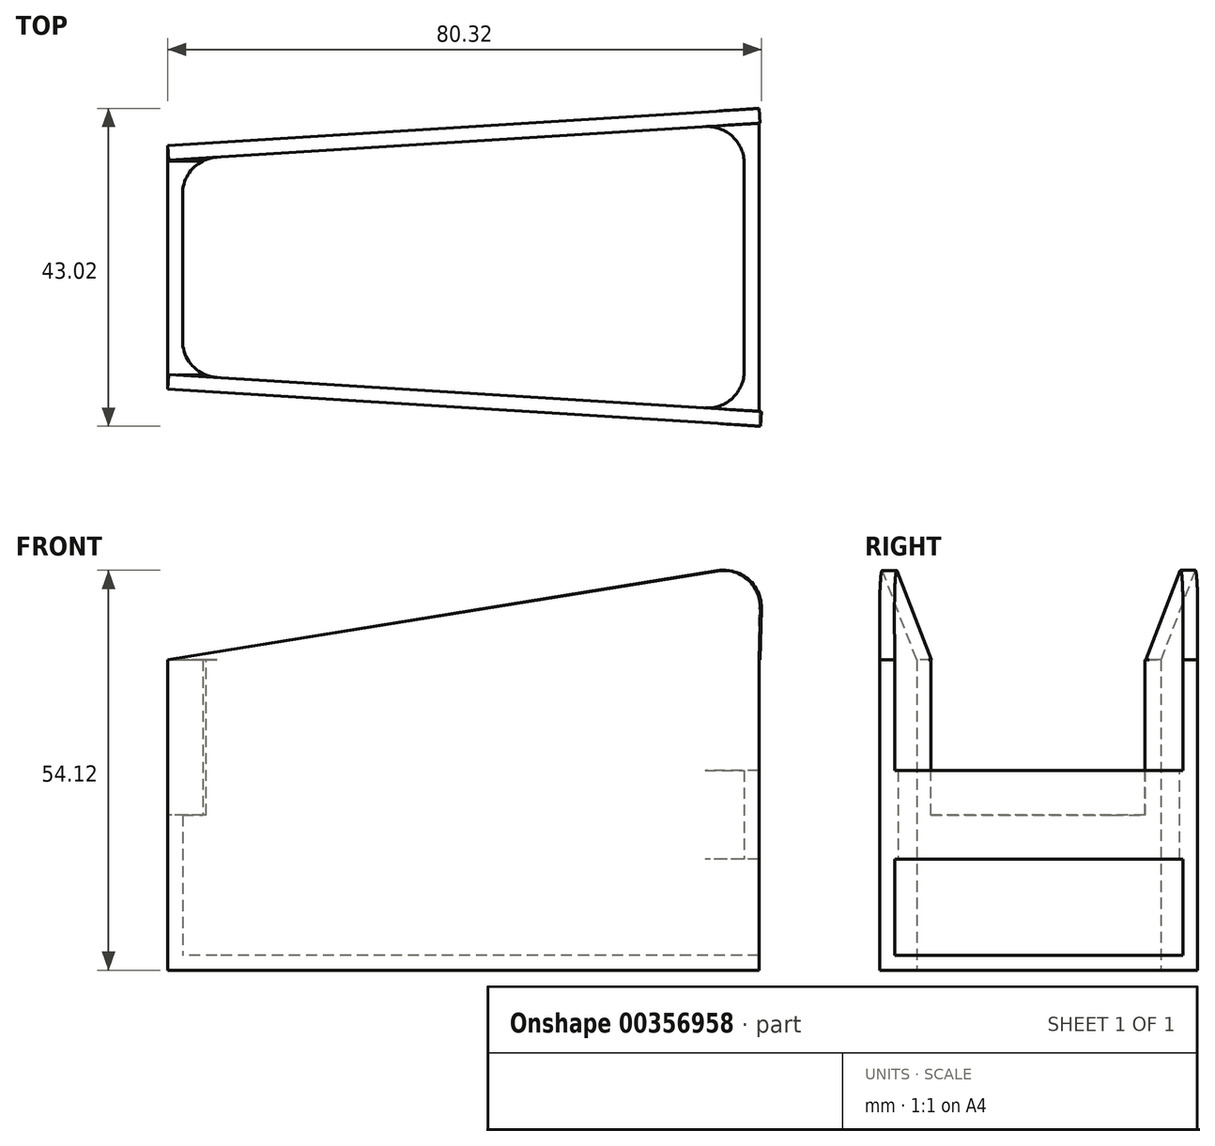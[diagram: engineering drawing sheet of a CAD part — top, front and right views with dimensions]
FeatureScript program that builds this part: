
annotation { "Feature Type Name" : "Feature", "Feature Type Description" : "" }
export const myFeature = defineFeature(function(context is Context, id is Id, definition is map)
    precondition{}
    {
        {
            var Q0;
            Q0=qCreatedBy(makeId("Top.planeOp"),FACE);
            var sketch = newSketch(context, id + "F0", { "sketchPlane" : qUnion([Q0])});
            skLineSegment(sketch, "E0", {"start": v(-65.37, 35.18) * mm, "end": v(-2.44, 35.18) * mm, "construction": true});
            skLineSegment(sketch, "E1", {"start": v(18.9, 56.68) * mm, "end": v(18.9, 13.68) * mm, "construction": true});
            skLineSegment(sketch, "E2", {"start": v(-61.1, 51.68) * mm, "end": v(-61.1, 18.68) * mm, "construction": true});
            skLineSegment(sketch, "E3", {"start": v(-2.44, 35.18) * mm, "end": v(28.85, 35.18) * mm, "construction": true});
            skLineSegment(sketch, "E4", {"start": v(-61.1, 51.68) * mm, "end": v(18.9, 56.68) * mm});
            skLineSegment(sketch, "E5", {"start": v(18.9, 56.68) * mm, "end": v(18.9, 13.68) * mm});
            skLineSegment(sketch, "E6", {"start": v(-61.1, 18.68) * mm, "end": v(18.9, 13.68) * mm});
            skLineSegment(sketch, "E7", {"start": v(-61.1, 51.68) * mm, "end": v(-61.1, 18.68) * mm});
            skLineSegment(sketch, "E8.0", {"start": v(-60.97, 49.68) * mm, "end": v(19.03, 54.68) * mm, "construction": true});
            skLineSegment(sketch, "E9.0", {"start": v(-60.97, 20.67) * mm, "end": v(19.03, 15.67) * mm});
            skLineSegment(sketch, "E10.0", {"start": v(16.9, 56.68) * mm, "end": v(16.9, 56.55) * mm});
            skLineSegment(sketch, "E11.0", {"start": v(-59.1, 49.8) * mm, "end": v(-59.1, 20.56) * mm});
            skLineSegment(sketch, "E12", {"start": v(-59.1, 49.8) * mm, "end": v(16.9, 54.55) * mm});
            skLineSegment(sketch, "E13.trimOffspring", {"start": v(16.9, 54.55) * mm, "end": v(16.9, 15.8) * mm});
            skLineSegment(sketch, "E14.trimOffspring", {"start": v(16.9, 13.8) * mm, "end": v(16.9, 13.68) * mm});
            skLineSegment(sketch, "E15", {"start": v(16.9, 54.55) * mm, "end": v(19.03, 54.68) * mm});
            skLineSegment(sketch, "E16", {"start": v(-59.1, 49.8) * mm, "end": v(-60.97, 49.68) * mm});
            skSolve(sketch);
        }
        {
            var Q0;
            {var subQ6=sQuery(id+"F0.wireOp",EDGE,"E7");Q0=makeQuery(id+"F0.imprint","IMPRINT",FACE,{"disambiguationData":[TD([[makeQuery(id+"F0.imprint","IMPRINT",EDGE,{"derivedFrom":subQ6}),1.0]])]});}
            var Q1;
            {var subQ5=sQuery(id+"F0.wireOp",EDGE,"E13.trimOffspring");Q1=makeQuery(id+"F0.imprint","IMPRINT",FACE,{"disambiguationData":[TD([[makeQuery(id+"F0.imprint","IMPRINT",EDGE,{"derivedFrom":subQ5}),1.0]])]});}
            var Q2;
            {var subQ0=sQuery(id+"F0.wireOp",EDGE,"E11.0");Q2=makeQuery(id+"F0.imprint","IMPRINT",FACE,{"disambiguationData":[TD([[makeQuery(id+"F0.imprint","IMPRINT",EDGE,{"derivedFrom":subQ0}),1.0]])]});}
            extrude(context, id + "F1", {"entities" : qUnion([Q0, Q1, Q2]), "depth" : 2 * mm, "offsetDistance" : 25 * mm});
        }
        {
            var Q0;
            {var subQ6=sQuery(id+"F0.wireOp",EDGE,"E7");Q0=makeQuery(id+"F0.imprint","IMPRINT",FACE,{"disambiguationData":[TD([[makeQuery(id+"F0.imprint","IMPRINT",EDGE,{"derivedFrom":subQ6}),1.0]])]});}
            extrude(context, id + "F2", {"entities" : qUnion([Q0]), "operationType" : NewBodyOperationType.ADD, "depth" : 42 * mm, "offsetDistance" : 25 * mm});
        }
        {
            var Q0;
            {var subQ0=sQuery(id+"F0.wireOp",EDGE,"E6");Q0=makeQuery(id+"F2.boolean.opBoolean","MERGE",FACE,{"derivedFrom":[makeQuery(id+"F1.opExtrude","SWEPT_FACE",FACE,{"disambiguationData":[OSD([subQ0])]}),makeQuery(id+"F2.opExtrude","SWEPT_FACE",FACE,{"disambiguationData":[OSD([subQ0])]})]});}
            var sketch = newSketch(context, id + "F3", { "sketchPlane" : qUnion([Q0])});
            skLineSegment(sketch, "E17", {"start": v(-62.15, 42) * mm, "end": v(18.37, 55) * mm});
            skLineSegment(sketch, "E18", {"start": v(18.01, 42) * mm, "end": v(18.37, 55) * mm});
            skLineSegment(sketch, "E19", {"start": v(18.37, 55) * mm, "end": v(18.01, 0) * mm, "construction": true});
            skSolve(sketch);
        }
        {
            var Q0;
            {var subQ0=sQuery(id+"F0.wireOp",EDGE,"E5");Q0=makeQuery(id+"F2.boolean.opBoolean","MERGE",FACE,{"derivedFrom":[makeQuery(id+"F1.opExtrude","SWEPT_FACE",FACE,{"disambiguationData":[OSD([subQ0])]}),makeQuery(id+"F2.opExtrude","SWEPT_FACE",FACE,{"disambiguationData":[OSD([subQ0]),TDD([makeQuery(id+"F0.imprint","IMPRINT",EDGE,{"disambiguationData":[TD([[makeQuery(id+"F0.imprint","INTERSECT",VERTEX,{"derivedFrom":[sQuery(id+"F0.wireOp",EDGE,"E4"),subQ0]}),-1.0]])],"derivedFrom":subQ0})])]}),makeQuery(id+"F2.opExtrude","SWEPT_FACE",FACE,{"disambiguationData":[OSD([subQ0]),TDD([makeQuery(id+"F0.imprint","IMPRINT",EDGE,{"disambiguationData":[TD([[makeQuery(id+"F0.imprint","INTERSECT",VERTEX,{"derivedFrom":[subQ0,sQuery(id+"F0.wireOp",EDGE,"E6")]}),1.0]])],"derivedFrom":subQ0})])]})]});}
            var sketch = newSketch(context, id + "F4", { "sketchPlane" : qUnion([Q0])});
            skLineSegment(sketch, "E20", {"start": v(13.68, 42) * mm, "end": v(15.68, 42) * mm});
            skLineSegment(sketch, "E21", {"start": v(13.68, 62.32) * mm, "end": v(13.68, 42) * mm});
            skSolve(sketch);
        }
        {
            var Q0;
            Q0=makeQuery(id+"F3.imprint","IMPRINT",FACE,{"disambiguationData":[TD([[makeQuery(id+"F3.imprint","IMPRINT",EDGE,{"derivedFrom":sQuery(id+"F3.wireOp",EDGE,"E17")}),-1.0]])]});
            extrude(context, id + "F5", {"entities" : qUnion([Q0]), "operationType" : NewBodyOperationType.ADD, "oppositeDirection" : true, "depth" : 2 * mm, "offsetDistance" : 25 * mm});
        }
        {
            var Q0;
            {var subQ0=sQuery(id+"F0.wireOp",EDGE,"E4");Q0=makeQuery(id+"F2.boolean.opBoolean","MERGE",FACE,{"derivedFrom":[makeQuery(id+"F1.opExtrude","SWEPT_FACE",FACE,{"disambiguationData":[OSD([subQ0])]}),makeQuery(id+"F2.opExtrude","SWEPT_FACE",FACE,{"disambiguationData":[OSD([subQ0])]})]});}
            var sketch = newSketch(context, id + "F6", { "sketchPlane" : qUnion([Q0])});
            skLineSegment(sketch, "E22", {"start": v(-22.4, 42) * mm, "end": v(-22.4, 55) * mm});
            skLineSegment(sketch, "E23", {"start": v(-22.4, 55) * mm, "end": v(57.76, 42) * mm});
            skSolve(sketch);
        }
        {
            var Q0;
            Q0=makeQuery(id+"F6.imprint","IMPRINT",FACE,{"disambiguationData":[TD([[makeQuery(id+"F6.imprint","IMPRINT",EDGE,{"derivedFrom":sQuery(id+"F6.wireOp",EDGE,"E22")}),-1.0]])]});
            extrude(context, id + "F7", {"entities" : qUnion([Q0]), "operationType" : NewBodyOperationType.ADD, "oppositeDirection" : true, "depth" : 2 * mm, "offsetDistance" : 25 * mm});
        }
        {
            var Q0;
            {var subQ0=sQuery(id+"F0.wireOp",EDGE,"E7");Q0=makeQuery(id+"F2.boolean.opBoolean","MERGE",FACE,{"derivedFrom":[makeQuery(id+"F1.opExtrude","SWEPT_FACE",FACE,{"disambiguationData":[OSD([subQ0])]}),makeQuery(id+"F2.opExtrude","SWEPT_FACE",FACE,{"disambiguationData":[OSD([subQ0])]})]});}
            var sketch = newSketch(context, id + "F8", { "sketchPlane" : qUnion([Q0])});
            skLineSegment(sketch, "E24", {"start": v(-49.56, 21) * mm, "end": v(-49.56, 42) * mm});
            skLineSegment(sketch, "E25", {"start": v(-20.6, 21) * mm, "end": v(-20.6, 42) * mm});
            skLineSegment(sketch, "E26", {"start": v(-49.56, 21) * mm, "end": v(-20.6, 21) * mm});
            skPoint(sketch, "E27.orphan", {"position": v(-49.56, 0) * mm});
            skPoint(sketch, "E28.orphan", {"position": v(-20.6, 0) * mm});
            skLineSegment(sketch, "E29", {"start": v(-49.56, 42) * mm, "end": v(-20.6, 42) * mm});
            skSolve(sketch);
        }
        {
            var Q0;
            Q0=makeQuery(id+"F8.imprint","IMPRINT",FACE,{"disambiguationData":[TD([[makeQuery(id+"F8.imprint","IMPRINT",EDGE,{"derivedFrom":sQuery(id+"F8.wireOp",EDGE,"E24")}),-1.0]])]});
            extrude(context, id + "F9", {"entities" : qUnion([Q0]), "operationType" : NewBodyOperationType.REMOVE, "oppositeDirection" : true, "depth" : 25 * mm, "offsetDistance" : 25 * mm});
        }
        {
            var Q0;
            Q0=makeQuery(id+"F4.imprint","IMPRINT",FACE,{"disambiguationData":[TD([[makeQuery(id+"F4.imprint","IMPRINT",EDGE,{"derivedFrom":sQuery(id+"F4.wireOp",EDGE,"E20")}),1.0]])]});
            var sketch = newSketch(context, id + "F10", { "sketchPlane" : qUnion([Q0])});
            skLineSegment(sketch, "E30", {"start": v(15.51, 15) * mm, "end": v(55.08, 15) * mm});
            skLineSegment(sketch, "E31.0", {"start": v(15.51, 27) * mm, "end": v(55.08, 27) * mm});
            skLineSegment(sketch, "E32", {"start": v(15.51, 27) * mm, "end": v(15.51, 15) * mm});
            skLineSegment(sketch, "E33", {"start": v(55.08, 27) * mm, "end": v(55.08, 15) * mm});
            skSolve(sketch);
        }
        {
            var Q0;
            {var subQ0=sQuery(id+"F10.wireOp",EDGE,"E30");var subQ1=sQuery(id+"F0.wireOp",EDGE,"E5");var subQ2=makeQuery(id+"F4.imprint","IMPRINT",EDGE,{"derivedFrom":makeQuery(id+"F2.opExtrude","SWEPT_EDGE",EDGE,{"disambiguationData":[OSD([subQ1,sQuery(id+"F0.wireOp",EDGE,"E9.0")])]})});var subQ3=makeQuery(id+"F10.imprint","INTERSECT",VERTEX,{"derivedFrom":[subQ2,subQ0]});Q0=makeQuery(id+"F10.imprint","IMPRINT",FACE,{"disambiguationData":[TD([[makeQuery(id+"F10.imprint","IMPRINT",EDGE,{"disambiguationData":[TD([[subQ3,-1.0]])],"derivedFrom":subQ0}),1.0]])]});}
            extrude(context, id + "F11", {"entities" : qUnion([Q0]), "operationType" : NewBodyOperationType.ADD, "oppositeDirection" : true, "depth" : 2 * mm, "offsetDistance" : 25 * mm});
        }
        {
            var Q0;
            {var subQ0=sQuery(id+"F0.wireOp",EDGE,"E9.0");Q0=makeQuery(id+"F11.boolean.opBoolean","INTERSECT",EDGE,{"derivedFrom":[makeQuery(id+"F5.boolean.opBoolean","MERGE",FACE,{"derivedFrom":[makeQuery(id+"F2.opExtrude","SWEPT_FACE",FACE,{"disambiguationData":[OSD([subQ0])]}),makeQuery(id+"F5.opExtrude","CAP_FACE",FACE,{"disambiguationData":[OSD([sQuery(id+"F0.wireOp",EDGE,"E6"),sQuery(id+"F3.wireOp",EDGE,"E17"),sQuery(id+"F3.wireOp",EDGE,"E18")])],"isStart":false})]}),makeQuery(id+"F11.opExtrude","CAP_FACE",FACE,{"disambiguationData":[OSD([sQuery(id+"F0.wireOp",EDGE,"E5"),subQ0,sQuery(id+"F0.wireOp",EDGE,"E15"),sQuery(id+"F10.wireOp",EDGE,"E30"),sQuery(id+"F10.wireOp",EDGE,"E31.0")])],"isStart":false})]});}
            var Q1;
            {var subQ0=sQuery(id+"F0.wireOp",EDGE,"E15");Q1=makeQuery(id+"F11.boolean.opBoolean","INTERSECT",EDGE,{"derivedFrom":[makeQuery(id+"F7.boolean.opBoolean","MERGE",FACE,{"derivedFrom":[makeQuery(id+"F2.opExtrude","SWEPT_FACE",FACE,{"disambiguationData":[OSD([sQuery(id+"F0.wireOp",EDGE,"E12"),subQ0])]}),makeQuery(id+"F7.opExtrude","CAP_FACE",FACE,{"disambiguationData":[OSD([sQuery(id+"F0.wireOp",EDGE,"E4"),sQuery(id+"F6.wireOp",EDGE,"E22"),sQuery(id+"F6.wireOp",EDGE,"E23")])],"isStart":false})]}),makeQuery(id+"F11.opExtrude","CAP_FACE",FACE,{"disambiguationData":[OSD([sQuery(id+"F0.wireOp",EDGE,"E5"),sQuery(id+"F0.wireOp",EDGE,"E9.0"),subQ0,sQuery(id+"F10.wireOp",EDGE,"E30"),sQuery(id+"F10.wireOp",EDGE,"E31.0")])],"isStart":false})]});}
            var Q2;
            Q2=makeQuery(id+"F2.opExtrude","SWEPT_EDGE",EDGE,{"disambiguationData":[OSD([sQuery(id+"F0.wireOp",EDGE,"E9.0"),sQuery(id+"F0.wireOp",EDGE,"E11.0")])]});
            var Q3;
            Q3=makeQuery(id+"F2.opExtrude","SWEPT_EDGE",EDGE,{"disambiguationData":[OSD([sQuery(id+"F0.wireOp",EDGE,"E11.0"),sQuery(id+"F0.wireOp",EDGE,"E12")])]});
            fillet(context, id + "F12", {"entities" : qUnion([Q0, Q1, Q2, Q3]), "radius" : 5 * mm, "tangentPropagation" : true, "allowEdgeOverflow" : false});
        }
        {
            var Q0;
            Q0=makeQuery(id+"F7.opExtrude","SWEPT_EDGE",EDGE,{"disambiguationData":[OSD([sQuery(id+"F6.wireOp",EDGE,"E22"),sQuery(id+"F6.wireOp",EDGE,"E23")])]});
            var Q1;
            Q1=makeQuery(id+"F5.opExtrude","SWEPT_EDGE",EDGE,{"disambiguationData":[OSD([sQuery(id+"F3.wireOp",EDGE,"E17"),sQuery(id+"F3.wireOp",EDGE,"E18")])]});
            fillet(context, id + "F13", {"entities" : qUnion([Q0, Q1]), "radius" : 5 * mm, "tangentPropagation" : true, "allowEdgeOverflow" : false});
        }
    });
